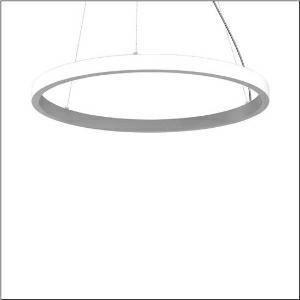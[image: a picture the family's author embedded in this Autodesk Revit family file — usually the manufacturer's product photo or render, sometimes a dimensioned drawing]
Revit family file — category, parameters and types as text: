
# Revit family: silica_21_ring-o_5pjbo4d1204a
name_source: partatom
category: Lighting Fixtures
units: mm (PartAtom-declared; Revit-internal decimal feet)

## family parameters
Cut with Voids When Loaded = No
Host = Face
Light Source = No
Part Type = Normal
Room Calculation Point = No
Round Connector Dimension = Use Diameter
Shared = No

## types (1)
- Silica 21 Ring-O (1 x LED, 8820 lm, 343 W, 3000K)
    Apparent Load = 343 VA
    CIE Flux Codes = 2 16 49 50 100
    Color Rendering = 80
    Color Temperature = 3000K
    Default Elevation = 1800 mm
    Description = Silica 21 Ring-O, suspended luminaire, of PMMA, frosted, light emission: outer ring side luminous distribution, primary light characteristic: symmetric, installation type: suspended mounting, LED, rated luminous flux: 8.820lm, luminous efficacy: 63lm/W, light colour: 830, colour temperature: 3000K, control gear: DALI 2, with terminal, 5-pole, mains connection: 230V, AC/DC, 0/50..60Hz, rated input power: 140W, housing, of extruded aluminium section, metallic grey (RAL 9006), diameter: 1.480mm, ceiling canopy, metallic grey (RAL 9006), protection rating (lamp compartment): IP40, insulation class (complete): insulation class I (protective earthing), certification: CE, impact resistance: IK02, permissible operating ambient temperature: 0..+35°C, packaging unit: 1 piece
    Height = 48 mm  [stored 0.15748 ft]
    Lamp = 1 x LED
    Lamp Light Flux = 8820 lm
    Lamp Power = 343 W
    Lamp count = 1
    Length = 1480 mm
    Luminous efficacy = 26 lm/W
    Manufacturer = Siteco
    ModVariant = No
    Model = 5PJBO4D1204A
    Mounting Place = Ceiling
    Mounting Type = Pendant
    Number of Poles = 1
    OnlyDefault = Yes
    Power Factor = 1
    Product Name = Silica 21 Ring-O
    Product group = suspended luminaire
    ProductGroupID = 904
    Protection Class = Protection class I
    Protection Degree = IP 40
    RLX_Detail_Level = 1
    RLX_Emergency_Light_Flux = 0 lm
    RLX_Emergency_Type = 0
    RLX_Emergency_Type_DB = No
    RlxData = <blob elided: 18405 chars, md5=5de80fc7>
    Socket = socket
    Standby Power = 0 W
    System Light Flux = 8819 lm
    System Power = 343 W
    Type Comments = Product without accessories
    Type Image = l_1251764.jpg
    URL = http://relux.com
    VarID = ---
    Voltage = 0 V
    Weight = 0.00 kg
    Width = 0 mm  [stored 0 ft]

note: [stored X ft] marks values corroborated as IEEE doubles in the binary element streams (Revit-internal decimal feet)

## geometry (parser evidence)
native form markers: Blend x4, Sweep x13
no freeform markers — native parametric forms only
